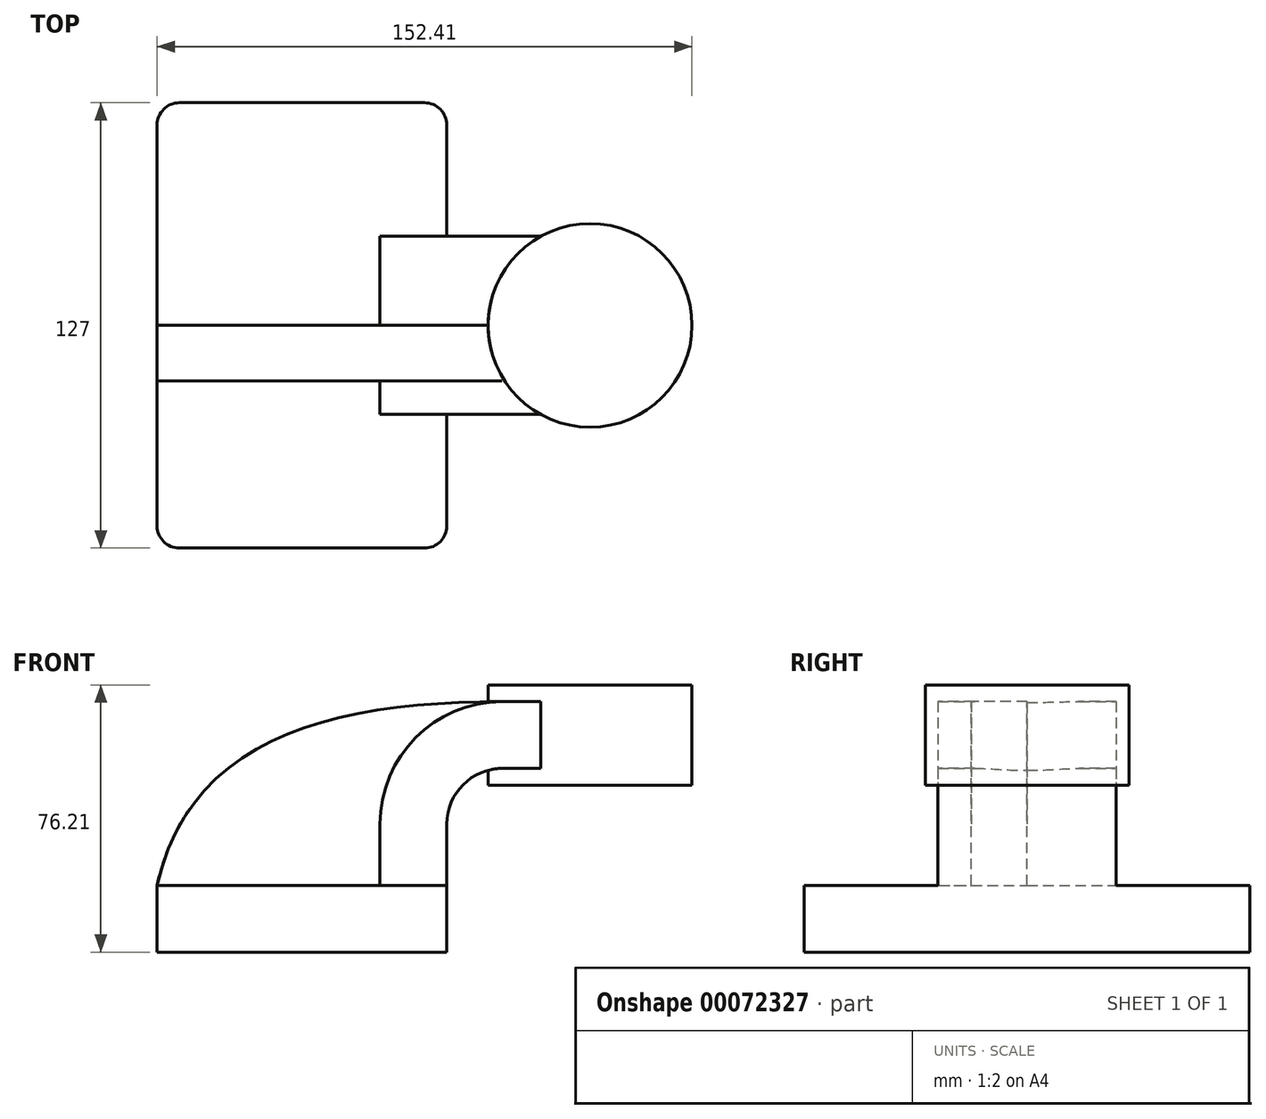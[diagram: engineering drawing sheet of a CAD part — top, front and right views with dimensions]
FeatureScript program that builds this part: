
annotation { "Feature Type Name" : "Feature", "Feature Type Description" : "" }
export const myFeature = defineFeature(function(context is Context, id is Id, definition is map)
    precondition{}
    {
        {
            var Q0;
            Q0=qCreatedBy(makeId("Front.planeOp"),FACE);
            var sketch = newSketch(context, id + "F0", { "sketchPlane" : qUnion([Q0])});
            skLineSegment(sketch, "E0.rect.bottom", {"start": v(-41.27, -9.53) * mm, "end": v(41.28, -9.53) * mm});
            skLineSegment(sketch, "E0.rect.top", {"start": v(-41.28, 9.53) * mm, "end": v(41.28, 9.53) * mm});
            skLineSegment(sketch, "E0.rect.left", {"start": v(-41.28, -9.53) * mm, "end": v(-41.28, 9.53) * mm});
            skLineSegment(sketch, "E0.rect.right", {"start": v(41.28, -9.53) * mm, "end": v(41.28, 9.53) * mm});
            skPoint(sketch, "E0.rect.middle", {"position": v(0, 0) * mm});
            skLineSegment(sketch, "E1.rect.bottom", {"start": v(60.33, 38.1) * mm, "end": v(111.12, 38.1) * mm});
            skLineSegment(sketch, "E1.rect.top", {"start": v(60.33, 66.67) * mm, "end": v(111.12, 66.67) * mm});
            skLineSegment(sketch, "E1.rect.left", {"start": v(60.33, 38.1) * mm, "end": v(60.33, 66.67) * mm});
            skLineSegment(sketch, "E1.rect.right", {"start": v(111.12, 38.1) * mm, "end": v(111.12, 66.67) * mm});
            skPoint(sketch, "E1.rect.middle", {"position": v(85.72, 52.39) * mm});
            skLineSegment(sketch, "E2", {"start": v(41.27, 9.53) * mm, "end": v(41.27, 26.99) * mm});
            skArc(sketch, "E3", {"start": v(41.27, 26.99) * mm, "mid": v(45.92, 38.21) * mm, "end": v(57.15, 42.86) * mm});
            skLineSegment(sketch, "E4", {"start": v(57.15, 42.86) * mm, "end": v(82.09, 42.86) * mm});
            skLineSegment(sketch, "E5.0", {"start": v(57.15, 61.91) * mm, "end": v(82.09, 61.91) * mm});
            skArc(sketch, "E5.1", {"start": v(22.23, 26.99) * mm, "mid": v(32.45, 51.68) * mm, "end": v(57.15, 61.91) * mm});
            skLineSegment(sketch, "E5.2", {"start": v(22.22, 9.53) * mm, "end": v(22.22, 26.99) * mm});
            skLineSegment(sketch, "E6", {"start": v(82.09, 38.1) * mm, "end": v(82.09, 66.67) * mm});
            skFitSpline(sketch, "E7", {"points": [v(-41.27, 9.52) * mm, v(57.15, 61.91) * mm], "startDerivative": vector(28.82, 127.87) * mm, "endDerivative": vector(143.3, 0.32) * mm});
            skSolve(sketch);
        }
        {
            var Q0;
            Q0=makeQuery(id+"F0.imprint","IMPRINT",FACE,{"disambiguationData":[TD([[makeQuery(id+"F0.imprint","IMPRINT",EDGE,{"derivedFrom":sQuery(id+"F0.wireOp",EDGE,"E0.rect.bottom")}),1.0]])]});
            extrude(context, id + "F1", {"entities" : qUnion([Q0]), "endBound" : BoundingType.SYMMETRIC, "depth" : 127 * mm});
        }
        {
            var Q0;
            {var subQ1=sQuery(id+"F0.wireOp",EDGE,"E2");Q0=makeQuery(id+"F0.imprint","IMPRINT",FACE,{"disambiguationData":[TD([[makeQuery(id+"F0.imprint","IMPRINT",EDGE,{"derivedFrom":subQ1}),1.0]])]});}
            var Q1;
            {var subQ0=sQuery(id+"F0.wireOp",EDGE,"E4");var subQ1=sQuery(id+"F0.wireOp",EDGE,"E1.rect.left");var subQ2=makeQuery(id+"F0.imprint","INTERSECT",VERTEX,{"derivedFrom":[subQ1,subQ0]});Q1=makeQuery(id+"F0.imprint","IMPRINT",FACE,{"disambiguationData":[TD([[makeQuery(id+"F0.imprint","IMPRINT",EDGE,{"disambiguationData":[TD([[subQ2,-1.0]])],"derivedFrom":subQ1}),-1.0]])]});}
            extrude(context, id + "F2", {"entities" : qUnion([Q0, Q1]), "operationType" : NewBodyOperationType.ADD, "endBound" : BoundingType.SYMMETRIC, "depth" : 50.8 * mm});
        }
        {
            var Q0;
            {var subQ3=sQuery(id+"F0.wireOp",EDGE,"E5.2");Q0=makeQuery(id+"F0.imprint","IMPRINT",FACE,{"disambiguationData":[TD([[makeQuery(id+"F0.imprint","IMPRINT",EDGE,{"derivedFrom":subQ3}),1.0]])]});}
            extrude(context, id + "F3", {"entities" : qUnion([Q0]), "operationType" : NewBodyOperationType.ADD, "depth" : 15.88 * mm});
        }
        {
            var Q0;
            {var subQ0=sQuery(id+"F0.wireOp",EDGE,"E1.rect.right");Q0=makeQuery(id+"F0.imprint","IMPRINT",FACE,{"disambiguationData":[TD([[makeQuery(id+"F0.imprint","IMPRINT",EDGE,{"derivedFrom":subQ0}),1.0]])]});}
            var Q1;
            Q1=sQuery(id+"F0.wireOp",EDGE,"E6");
            revolve(context, id + "F4", {"operationType" : NewBodyOperationType.ADD, "entities" : qUnion([Q0]), "axis" : qUnion([Q1]), "revolveType" : RevolveType.FULL});
        }
        {
            var Q0;
            Q0=makeQuery(id+"F1.opExtrude","CAP_EDGE",EDGE,{"disambiguationData":[OSD([sQuery(id+"F0.wireOp",EDGE,"E0.rect.right")])],"isStart":false});
            var Q1;
            Q1=makeQuery(id+"F1.opExtrude","CAP_EDGE",EDGE,{"disambiguationData":[OSD([sQuery(id+"F0.wireOp",EDGE,"E0.rect.left")])],"isStart":false});
            var Q2;
            Q2=makeQuery(id+"F1.opExtrude","CAP_EDGE",EDGE,{"disambiguationData":[OSD([sQuery(id+"F0.wireOp",EDGE,"E0.rect.right")])],"isStart":true});
            var Q3;
            Q3=makeQuery(id+"F1.opExtrude","CAP_EDGE",EDGE,{"disambiguationData":[OSD([sQuery(id+"F0.wireOp",EDGE,"E0.rect.left")])],"isStart":true});
            fillet(context, id + "F5", {"entities" : qUnion([Q0, Q1, Q2, Q3]), "radius" : 6.35 * mm, "tangentPropagation" : true, "allowEdgeOverflow" : false});
        }
    });
